# Revit family: Base_Cabinets-Teknion-CEBWU_Base_Cabinet_Recycling_Disposal_Center-R2023
name_source: partatom
category: Furniture
units: mm (PartAtom-declared; Revit-internal decimal feet)

## family parameters
Always vertical = Yes
Cut with Voids When Loaded = No
Enable Cutting in Views = No
OmniClass Number = 23.40.20.00
OmniClass Title = General Furniture and Specialties
Render Appearance Source = Family Geometry
Room Calculation Point = No
Shared = Yes
Work Plane-Based = No

## types (3) — shared parameters
Actual Height = 35 "
Assembly Code = E2020200
Available Height = 35 Inch Only
Height = 35 "
Manufacturer = Teknion
Manufacturer Fax = 416.661.4586
Part Number = CEBWU
Product Documentation Link = https://www.teknion.com
Product Line = Base Cabinets
Product Page URL = https://www.teknion.com
Series = Expansion Casework+
Sustainability Data = https://www.teknion.com
URL = www.teknion.com
Unit Weight URL = http://www.teknion.com
Warranty = http://www.teknion.com
zero-valued in all types: Default Elevation

## per-type parameters (varying)
| type | 1 & 3 Bins | 2 & 3 Bins | 2D - 1 & 2 Bins | 2D - 1 & 3 Bins | Cut - 2 Doors | Cut - 3 Doors | Cut - Divider - 2 Bins | Cut - Divider - 3 Bins | Cut-Out - 1 & 3 Bin | Cut-Out - 2 & 3 Bin | Cut-Out - Front - 1 & 3 Doors | Cut-Out - Front - 2 & 3 Doors | D - Dual | Description | Divider - 2 Bins | Divider - 3 Bins | Model | S - Single | T - Triple |
| Triple Configuration | Yes | Yes | No | Yes | 0.2 " | 3 " | 0.2 " | 15 " | 2 " | 2 " | 1 " | 1 " | No | Base Cabinet - Recycling/Disposal Center, Triple Configuration, 35" Height, No Door Swing Direction | No | Yes | CEBWUT__35_N | No | Yes |
| Dual Configuration | No | Yes | Yes | No | 3 " | 0.2 " | 15 " | 0.2 " | 0.2 " | 2 " | 0.2 " | 1 " | Yes | Base Cabinet - Recycling/Disposal Center, Dual Configuration, 35" Height, No Door Swing Direction | Yes | No | CEBWUD__35_N | No | No |
| Single Configuration | Yes | No | Yes | Yes | 0.2 " | 0.2 " | 0.2 " | 0.2 " | 2 " | 0.2 " | 1 " | 0.2 " | No | Base Cabinet - Recycling/Disposal Center, Single Configuration, 35" Height | No | No | CEBWUS__35__ | Yes | No |

## geometry (parser evidence)
native form markers: Sweep x3
no freeform markers — native parametric forms only
